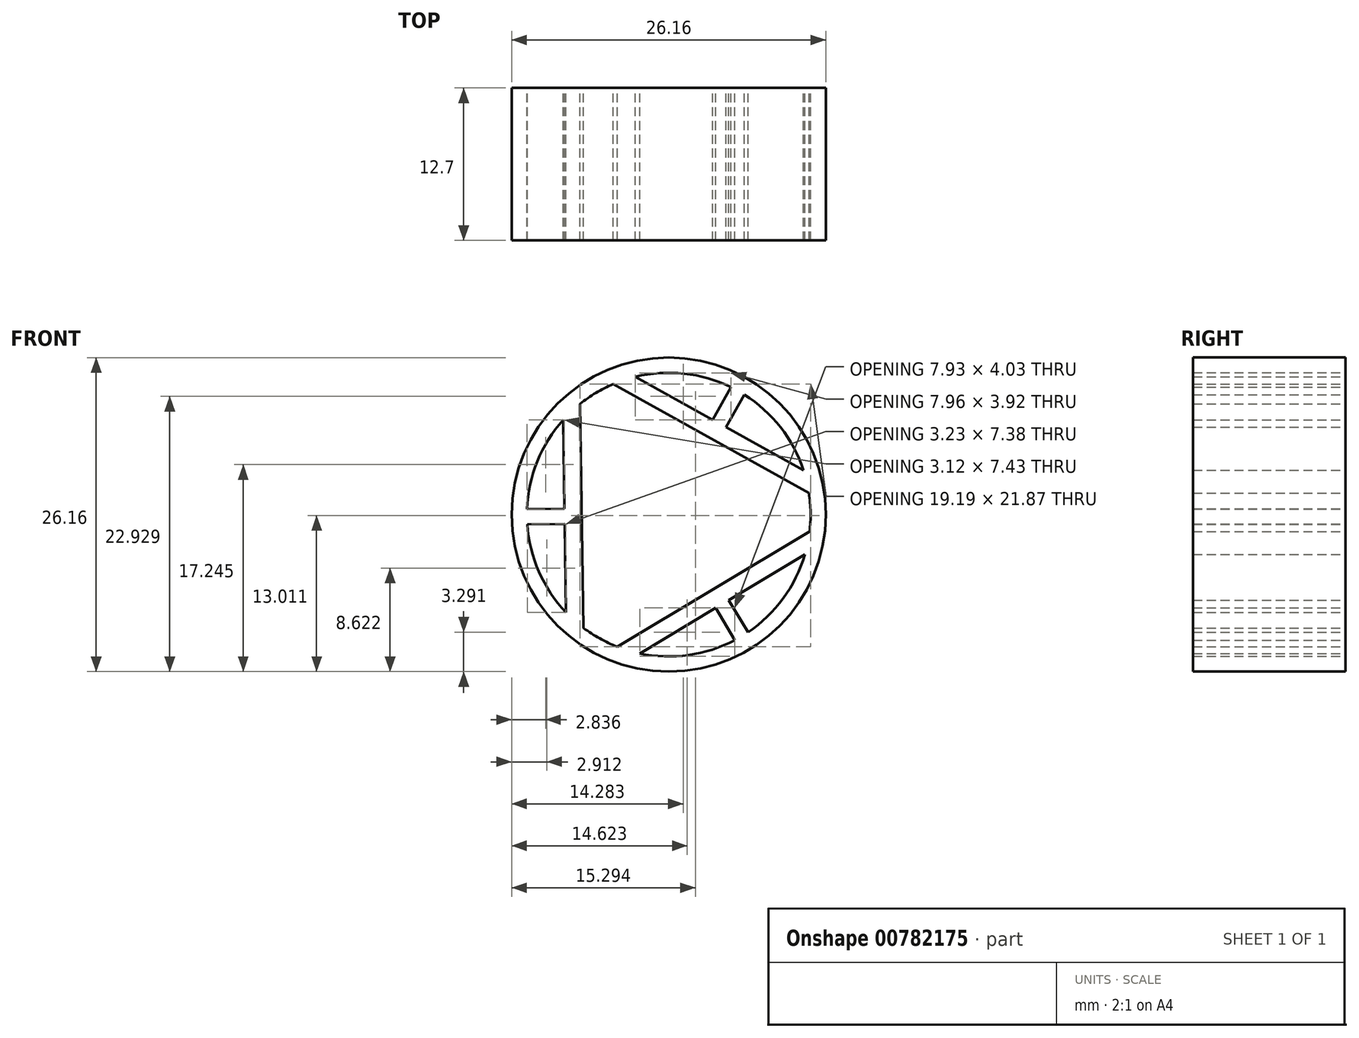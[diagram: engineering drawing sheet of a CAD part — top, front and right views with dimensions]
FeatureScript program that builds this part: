
annotation { "Feature Type Name" : "Feature", "Feature Type Description" : "" }
export const myFeature = defineFeature(function(context is Context, id is Id, definition is map)
    precondition{}
    {
        {
            var Q0;
            Q0=qCreatedBy(makeId("Front.planeOp"),FACE);
            var sketch = newSketch(context, id + "F0", { "sketchPlane" : qUnion([Q0])});
            skPoint(sketch, "E0.0.midPoint", {"position": v(0, 7.24) * mm});
            skCircle(sketch, "E1", {"center": v(0, 0) * mm, "radius": 13.08 * mm});
            skCircle(sketch, "E2.cCircle", {"center": v(0, 0) * mm, "radius": 7.24 * mm, "construction": true});
            skLineSegment(sketch, "E2.0", {"start": v(11.73, -1.42) * mm, "end": v(-4.3, -11) * mm});
            skLineSegment(sketch, "E2.2", {"start": v(-4.63, 10.87) * mm, "end": v(11.68, 1.78) * mm});
            skPoint(sketch, "E2.0.midPoint", {"position": v(3.72, -6.21) * mm});
            skArc(sketch, "E3", {"start": v(11.73, -1.42) * mm, "mid": v(11.8, 0.18) * mm, "end": v(11.68, 1.78) * mm});
            skPoint(sketch, "E4.orphan", {"position": v(-7.43, 12.42) * mm});
            skPoint(sketch, "E5.orphan", {"position": v(14.48, 0.22) * mm});
            skLineSegment(sketch, "E6.trimOffspring", {"start": v(-7.1, -9.44) * mm, "end": v(-7.38, 9.22) * mm});
            skPoint(sketch, "E2.1.start.orphan", {"position": v(-7.04, -12.65) * mm});
            skArc(sketch, "E7.trimOffspring", {"start": v(-4.63, 10.87) * mm, "mid": v(-6.06, 10.14) * mm, "end": v(-7.38, 9.22) * mm});
            skArc(sketch, "E8.trimOffspring", {"start": v(-7.1, -9.44) * mm, "mid": v(-5.75, -10.32) * mm, "end": v(-4.3, -11) * mm});
            skArc(sketch, "E9", {"start": v(-2.42, -11.56) * mm, "mid": v(1.64, -11.7) * mm, "end": v(5.5, -10.45) * mm});
            skLineSegment(sketch, "E10", {"start": v(-2.42, -11.56) * mm, "end": v(3.9, -7.77) * mm});
            skLineSegment(sketch, "E11.1.0", {"start": v(11.22, 3.68) * mm, "end": v(4.78, 7.27) * mm});
            skArc(sketch, "E11.1.1", {"start": v(11.22, 3.68) * mm, "mid": v(9.3, 7.27) * mm, "end": v(6.3, 10) * mm});
            skLineSegment(sketch, "E11.2.0", {"start": v(-8.8, 7.88) * mm, "end": v(-8.69, 0.5) * mm});
            skArc(sketch, "E11.2.1", {"start": v(-8.8, 7.88) * mm, "mid": v(-10.95, 4.43) * mm, "end": v(-11.8, 0.45) * mm});
            skLineSegment(sketch, "E12", {"start": v(3.9, -7.77) * mm, "end": v(5.5, -10.45) * mm});
            skLineSegment(sketch, "E13", {"start": v(5, -7.12) * mm, "end": v(6.6, -9.8) * mm});
            skLineSegment(sketch, "E14.trimOffspring", {"start": v(5, -7.12) * mm, "end": v(11.33, -3.33) * mm});
            skArc(sketch, "E15.trimOffspring", {"start": v(6.6, -9.8) * mm, "mid": v(9.53, -6.98) * mm, "end": v(11.33, -3.33) * mm});
            skLineSegment(sketch, "E16.1.0", {"start": v(4.78, 7.27) * mm, "end": v(6.3, 10) * mm});
            skLineSegment(sketch, "E16.1.1", {"start": v(3.67, 7.89) * mm, "end": v(5.18, 10.61) * mm});
            skLineSegment(sketch, "E16.2.0", {"start": v(-8.69, 0.5) * mm, "end": v(-11.8, 0.45) * mm});
            skLineSegment(sketch, "E16.2.1", {"start": v(-8.67, -0.77) * mm, "end": v(-11.78, -0.82) * mm});
            skArc(sketch, "E17.trimOffspring", {"start": v(5.18, 10.61) * mm, "mid": v(1.28, 11.74) * mm, "end": v(-2.78, 11.48) * mm});
            skLineSegment(sketch, "E18.trimOffspring", {"start": v(3.67, 7.89) * mm, "end": v(-2.78, 11.48) * mm});
            skLineSegment(sketch, "E19.trimOffspring", {"start": v(-8.67, -0.77) * mm, "end": v(-8.55, -8.15) * mm});
            skArc(sketch, "E20.trimOffspring", {"start": v(-11.78, -0.82) * mm, "mid": v(-10.8, -4.76) * mm, "end": v(-8.55, -8.15) * mm});
            skSolve(sketch);
        }
        {
            var Q0;
            Q0 = qSketchRegion(id + "F0", true);
            extrude(context, id + "F1", {"entities" : qUnion([Q0]), "depth" : 12.7 * mm, "offsetDistance" : 25.4 * mm});
        }
    });
